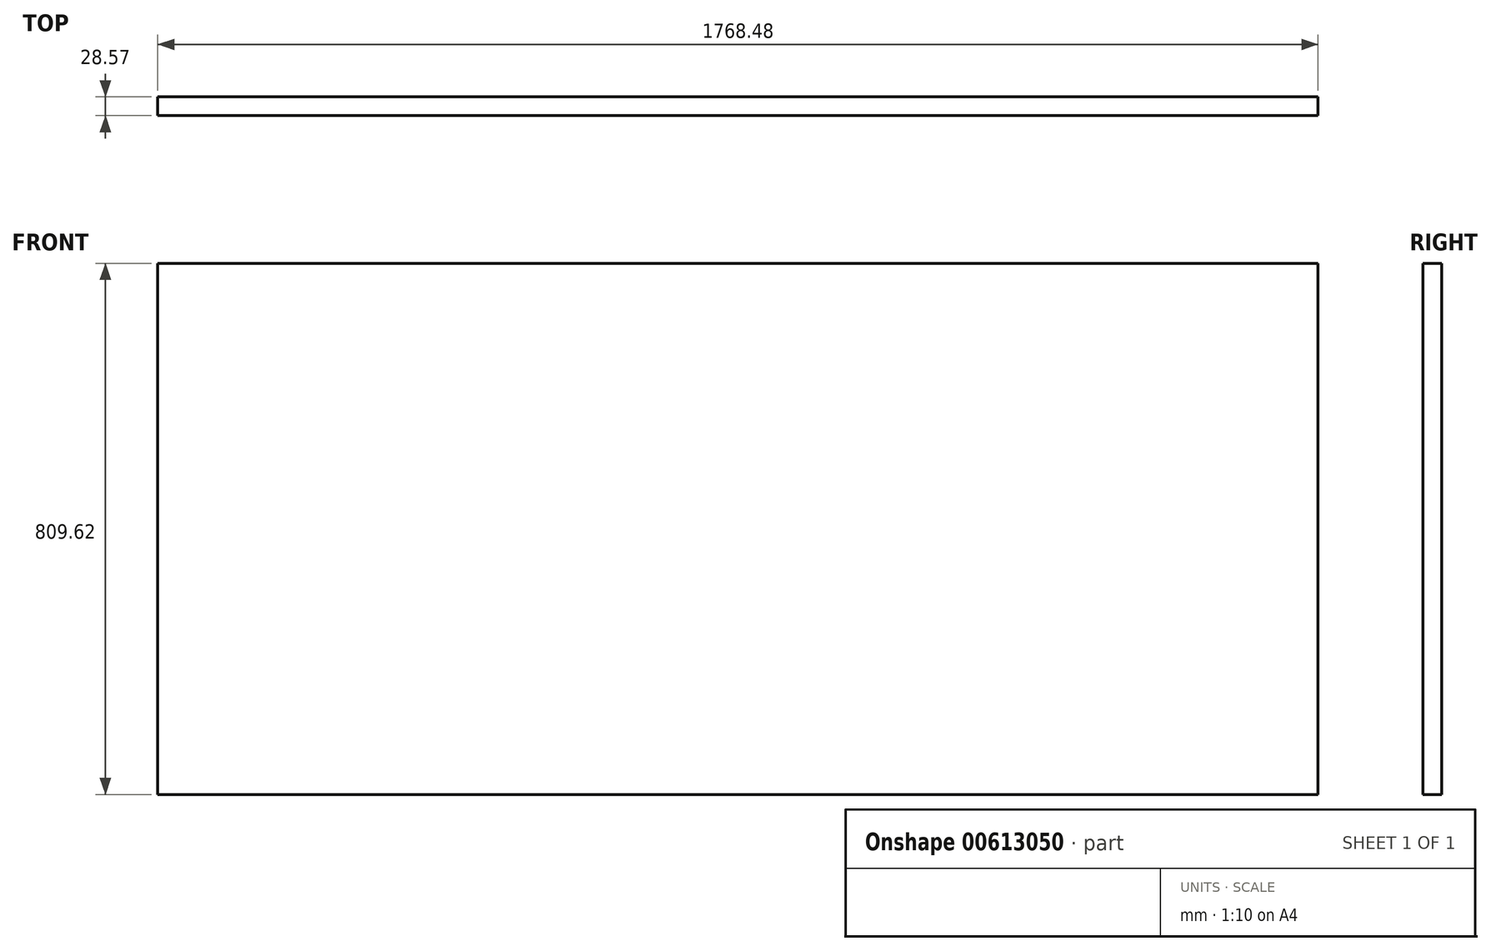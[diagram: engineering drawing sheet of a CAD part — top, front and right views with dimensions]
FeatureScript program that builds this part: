
annotation { "Feature Type Name" : "Feature", "Feature Type Description" : "" }
export const myFeature = defineFeature(function(context is Context, id is Id, definition is map)
    precondition{}
    {
        {
            var Q0;
            Q0=qCreatedBy(makeId("Front.planeOp"),FACE);
            var sketch = newSketch(context, id + "F0", { "sketchPlane" : qUnion([Q0])});
            skLineSegment(sketch, "E0.bottom", {"start": v(884.24, 404.81) * mm, "end": v(-884.24, 404.81) * mm});
            skLineSegment(sketch, "E0.top", {"start": v(884.24, -404.81) * mm, "end": v(-884.24, -404.81) * mm});
            skLineSegment(sketch, "E0.left", {"start": v(884.24, 404.81) * mm, "end": v(884.24, -404.81) * mm});
            skLineSegment(sketch, "E0.right", {"start": v(-884.24, 404.81) * mm, "end": v(-884.24, -404.81) * mm});
            skPoint(sketch, "E0.middle", {"position": v(0, 0) * mm});
            skSolve(sketch);
        }
        {
            var Q0;
            Q0 = qSketchRegion(id + "F0", true);
            extrude(context, id + "F1", {"entities" : qUnion([Q0]), "depth" : 28.57 * mm, "offsetDistance" : 25.4 * mm});
        }
    });
